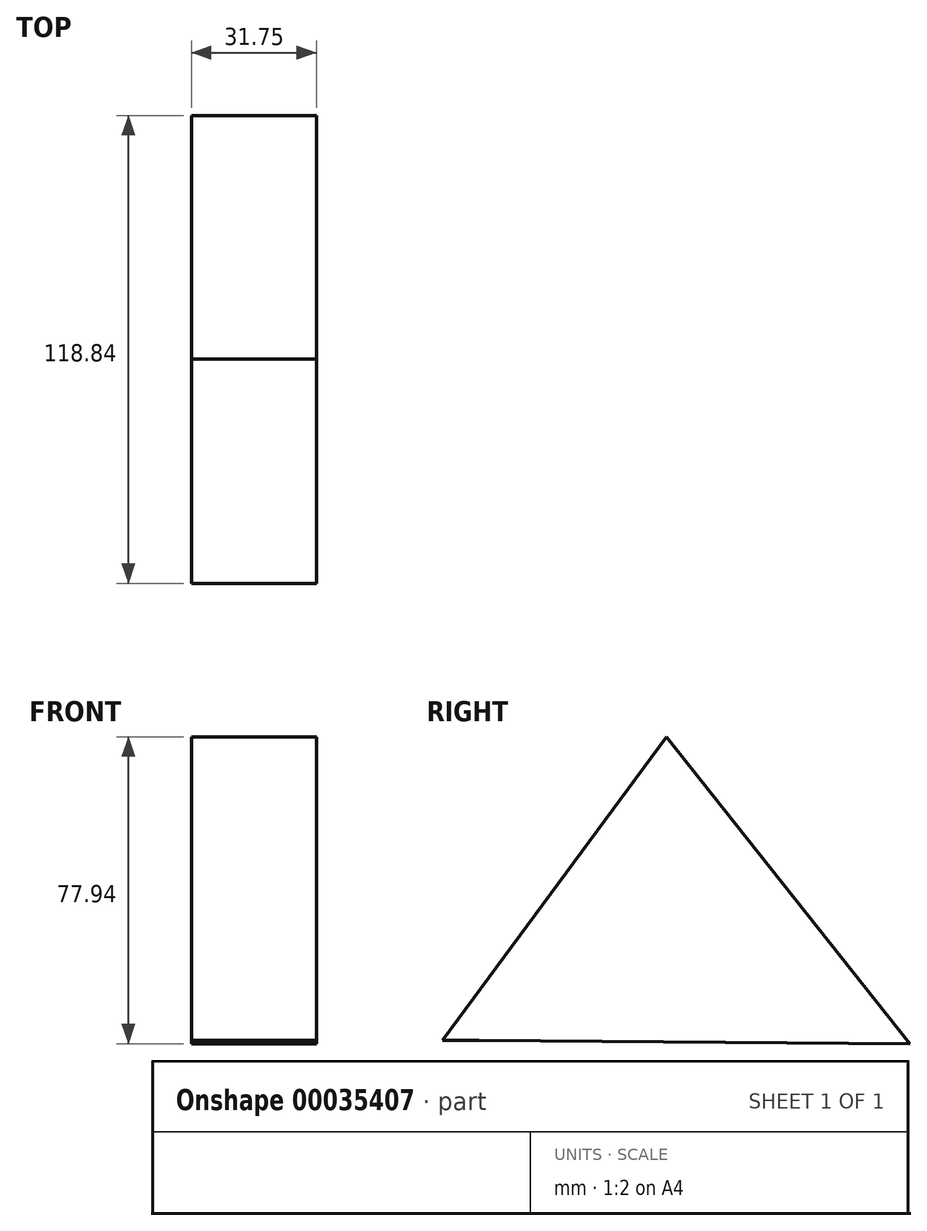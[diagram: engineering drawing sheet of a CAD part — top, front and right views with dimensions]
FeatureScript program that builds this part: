
annotation { "Feature Type Name" : "Feature", "Feature Type Description" : "" }
export const myFeature = defineFeature(function(context is Context, id is Id, definition is map)
    precondition{}
    {
        {
            var Q0;
            Q0=qCreatedBy(makeId("Right.planeOp"),FACE);
            var sketch = newSketch(context, id + "F0", { "sketchPlane" : qUnion([Q0])});
            skLineSegment(sketch, "E0", {"start": v(-56.98, -31.54) * mm, "end": v(0, 45.58) * mm});
            skLineSegment(sketch, "E1", {"start": v(0, 45.58) * mm, "end": v(61.86, -32.36) * mm});
            skLineSegment(sketch, "E2", {"start": v(61.86, -32.36) * mm, "end": v(-47.62, -31.54) * mm});
            skLineSegment(sketch, "E3", {"start": v(-47.62, -31.54) * mm, "end": v(-56.98, -31.54) * mm});
            skSolve(sketch);
        }
        {
            var Q0;
            Q0=makeQuery(id+"F0.imprint","IMPRINT",FACE,{"disambiguationData":[TD([[makeQuery(id+"F0.imprint","IMPRINT",EDGE,{"derivedFrom":sQuery(id+"F0.wireOp",EDGE,"E0")}),-1.0]])]});
            extrude(context, id + "F1", {"entities" : qUnion([Q0]), "depth" : 31.75 * mm});
        }
    });
